# Revit family: NBS_Allermuir_OffcChrs-en-us-Folk_HighStool
name_source: partatom
category: Furniture
revit_build: Autodesk Revit 2018 (Build: 20190510_1515(x64)
units: mm (PartAtom-declared; Revit-internal decimal feet)

## family parameters
Always vertical = Yes
Cut with Voids When Loaded = No
Room Calculation Point = No
Shared = No
Work Plane-Based = No

## types (2) — shared parameters
AssetType = Movable
Category = Pr_40_50_12_57:Office chairs
CodePerformance = BS EN 16139 level 1
Color = Off black, White, Crayon gray, Pistachio, Seattle green, Aubergine
DurationUnit = year
ExpectedLife = 10
Features = Beech ply seat with a clear finish, Beech ply back with a clear finish, Cast Aluminum frame finished in Off-Black powder coat, Solid Beech legs with a clear finish, Plastic glides, Footrest finished in Off-Black powdercoat, Footrest protector, Cast Aluminum frame available in White, Crayon Gray, Pistachio, Aubergine or Seattle Green powdercoat, Beech ply seat, back and solid Beech legs available in Off-Black, White, Crayon Gray, Pistachio, Aubergine and Seattle Green colorwash or stained, Oak ply seat, back and solid Oak legs with a clear finish, Oak ply seat and back with a clear finish, Plastic glides with felt
Finish = Off-Black powder coat, White powder coat, Crayon Gray powder coat, Pistachio powder coat, Seattle Green powder coat, Aubergine powder coat, Off-Black plastic, White plastic, Crayon Gray plastic, Pistachio plastic, Seattle Green plastic, Aubergine plastic, Clear Beech, Clear Oak, American Cherry, American Walnut, Dark Walnut, Wenge, Off-Black color wash, White color wash, Crayon Gray color wash, Pistachio color wash, Seattle Green color wash, Aubergine color wash
FrameFinish = Off black, White, Crayon grey, Pistachio, Seattle green, Aubergine
FrameMaterial = NBS_Allermuir_Aluminium_BlackPowderCoat
IfcExportAs = IfcFurnitureType
IfcExportType = STOOL
IsBuiltIn = No
LegMaterial = NBS_Allermuir_Beech_ClearFinish
ManufacturerName = Allermuir
ManufacturerURL = www.allermuir.com
ModelReference = Folk_HighStool
NBSCertification = www.nationalbimlibrary.com/cert/fa1mtgmb
NBSDescription = Office chairs
NBSReference = 45-35-20/330
NominalDepth = 21 "
NominalHeight = 43 "
NominalLength = 19 "
NominalWidth = 19 "
OmniClassCode = 22-12 52 23
OmniClassTitle = Office Seating
OmniClassVersion = Table 22 2012-05-16
ProductInformation = https://www.allermuir.com
SeatDepth = 17.25"
SeatHeight = 29.75"
SeatWidth = 18"
SeatingHeight = 30 "
Size = 20.5 x 43.25 x 19"
Status = UNSET
Style = Stool
SustainabilityPerformance = 99% recyclable
Uniclass2015Code = Pr_40_50_12_57
Uniclass2015Title = Office chairs
Uniclass2015Version = Products v1.15
Version = 1
WarrantyDescription = Allermuir warrant that its manufactured products are free from manufacturing defects - in materials or workmanship - for a period of ten (10) years. , Allermuir will repair, or replace (at Allermuir's sole discretion) with comparable free of charge materials / components, any product / component which fails under normal use in a single shift environment, as a result of a defect in the materials and/ or workmanship
WarrantyDurationParts = 10
WarrantyDurationUnit = year
WoodStains = Clear Oak, American Cherry, American Walnut, Dark Walnut, Wenge
zero-valued in all types: HighestSeatingHeight, LowestSeatingHeight

## per-type parameters (varying)
| type | BIMObjectName | Description | Material | ModelNumber | Name | SeatMaterial |
| Folk_HighStool_FLK301 | NBS_Allermuir_OfficeChairs_Folk_HighStool_FLK301-US | Stool - Wood seat and back | Oak, aluminium | FLK301 | OfficeChairs_FLK301_Folk_Allermuir | NBS_Allermuir_Beech_ClearFinish |
| Folk_HighStool_FLK303 | NBS_Allermuir_OfficeChairs_Folk_HighStool_FLK303-US | Stool - Plastic seat and back | Plastic, aluminium | FLK303 | OfficeChairs_FLK303_Folk_Allermuir | NBS_Allermuir_Plastic_Black |

## geometry (parser evidence)
native form markers: Sweep x5
no freeform markers — native parametric forms only
